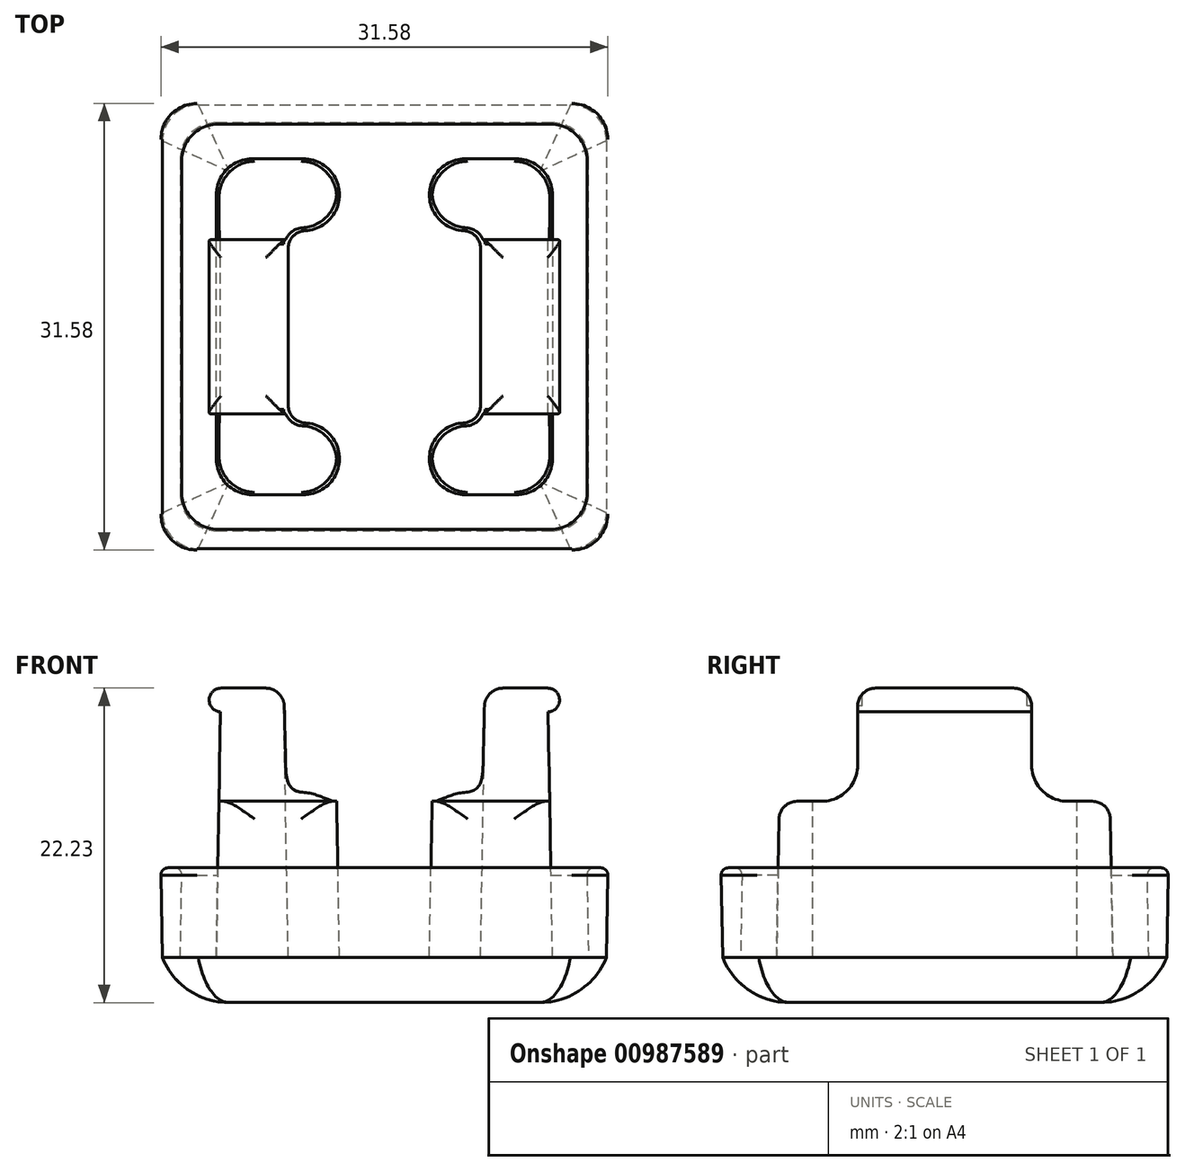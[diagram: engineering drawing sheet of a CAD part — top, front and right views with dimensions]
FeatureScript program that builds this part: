
annotation { "Feature Type Name" : "Feature", "Feature Type Description" : "" }
export const myFeature = defineFeature(function(context is Context, id is Id, definition is map)
    precondition{}
    {
        {
            var Q0;
            Q0=qCreatedBy(makeId("Top.planeOp"),FACE);
            var sketch = newSketch(context, id + "F0", { "sketchPlane" : qUnion([Q0])});
            skLineSegment(sketch, "E0.bottom", {"start": v(-15.68, 15.68) * mm, "end": v(15.68, 15.68) * mm});
            skLineSegment(sketch, "E0.top", {"start": v(-15.68, -15.68) * mm, "end": v(15.68, -15.68) * mm});
            skLineSegment(sketch, "E0.left", {"start": v(-15.68, 15.68) * mm, "end": v(-15.68, -15.68) * mm});
            skLineSegment(sketch, "E0.right", {"start": v(15.68, 15.68) * mm, "end": v(15.68, -15.68) * mm});
            skLineSegment(sketch, "E1.bottom", {"start": v(-14.41, 14.41) * mm, "end": v(14.41, 14.41) * mm});
            skLineSegment(sketch, "E1.top", {"start": v(-14.41, -14.41) * mm, "end": v(14.41, -14.41) * mm});
            skLineSegment(sketch, "E1.left", {"start": v(-14.41, 14.41) * mm, "end": v(-14.41, -14.41) * mm});
            skLineSegment(sketch, "E1.right", {"start": v(14.41, 14.41) * mm, "end": v(14.41, -14.41) * mm});
            skLineSegment(sketch, "E2.bottom", {"start": v(-11.87, 11.87) * mm, "end": v(-3.17, 11.87) * mm});
            skLineSegment(sketch, "E2.top", {"start": v(-11.87, -11.87) * mm, "end": v(-3.17, -11.87) * mm});
            skLineSegment(sketch, "E2.left", {"start": v(-11.87, 11.87) * mm, "end": v(-11.87, -11.87) * mm});
            skLineSegment(sketch, "E2.right", {"start": v(11.87, 11.87) * mm, "end": v(11.87, -11.87) * mm});
            skLineSegment(sketch, "E3.bottom", {"start": v(-6.8, 6.8) * mm, "end": v(-3.17, 6.8) * mm});
            skLineSegment(sketch, "E3.top", {"start": v(-6.8, -6.8) * mm, "end": v(-3.18, -6.8) * mm});
            skLineSegment(sketch, "E3.left", {"start": v(-6.8, 6.8) * mm, "end": v(-6.8, -6.8) * mm});
            skLineSegment(sketch, "E3.right", {"start": v(6.8, 6.8) * mm, "end": v(6.8, -6.8) * mm});
            skLineSegment(sketch, "E4", {"start": v(-3.17, 6.8) * mm, "end": v(-3.18, 11.87) * mm});
            skLineSegment(sketch, "E5", {"start": v(3.17, 11.87) * mm, "end": v(3.18, 6.8) * mm});
            skLineSegment(sketch, "E6", {"start": v(-3.18, -6.8) * mm, "end": v(-3.18, -11.87) * mm});
            skLineSegment(sketch, "E7", {"start": v(3.18, -6.8) * mm, "end": v(3.18, -11.87) * mm});
            skLineSegment(sketch, "E8.trimOffspring", {"start": v(3.18, 6.8) * mm, "end": v(6.8, 6.8) * mm});
            skLineSegment(sketch, "E9.trimOffspring", {"start": v(3.18, 11.87) * mm, "end": v(11.87, 11.87) * mm});
            skLineSegment(sketch, "E10.trimOffspring", {"start": v(3.18, -6.8) * mm, "end": v(6.8, -6.8) * mm});
            skLineSegment(sketch, "E11.trimOffspring", {"start": v(3.18, -11.87) * mm, "end": v(11.87, -11.87) * mm});
            skSolve(sketch);
        }
        {
            var Q0;
            Q0=makeQuery(id+"F0.imprint","IMPRINT",FACE,{"disambiguationData":[TD([[makeQuery(id+"F0.imprint","IMPRINT",EDGE,{"derivedFrom":sQuery(id+"F0.wireOp",EDGE,"E2.bottom")}),-1.0]])]});
            var Q1;
            Q1=makeQuery(id+"F0.imprint","IMPRINT",FACE,{"disambiguationData":[TD([[makeQuery(id+"F0.imprint","IMPRINT",EDGE,{"derivedFrom":sQuery(id+"F0.wireOp",EDGE,"E2.right")}),-1.0]])]});
            extrude(context, id + "F1", {"entities" : qUnion([Q0, Q1]), "depth" : 19.05 * mm, "offsetDistance" : 25.4 * mm, "hasDraft" : true, "draftAngle" : 1 * degree, "draftPullDirection" : true});
        }
        {
            var Q0;
            Q0 = qSketchRegion(id + "F0", true);
            extrude(context, id + "F2", {"entities" : qUnion([Q0]), "depth" : 6.35 * mm, "offsetDistance" : 25.4 * mm, "hasDraft" : true, "draftAngle" : 1 * degree});
        }
        {
            var Q0;
            Q0 = qSketchRegion(id + "F0", true);
            var Q1;
            Q1=makeQuery(id+"F0.imprint","IMPRINT",FACE,{"disambiguationData":[TD([[makeQuery(id+"F0.imprint","IMPRINT",EDGE,{"derivedFrom":sQuery(id+"F0.wireOp",EDGE,"E2.bottom")}),-1.0]])]});
            var Q2;
            Q2=makeQuery(id+"F0.imprint","IMPRINT",FACE,{"disambiguationData":[TD([[makeQuery(id+"F0.imprint","IMPRINT",EDGE,{"derivedFrom":sQuery(id+"F0.wireOp",EDGE,"E2.right")}),-1.0]])]});
            var Q3;
            Q3=makeQuery(id+"F0.imprint","IMPRINT",FACE,{"disambiguationData":[TD([[makeQuery(id+"F0.imprint","IMPRINT",EDGE,{"derivedFrom":sQuery(id+"F0.wireOp",EDGE,"E1.bottom")}),-1.0]])]});
            extrude(context, id + "F3", {"entities" : qUnion([Q0, Q1, Q2, Q3]), "oppositeDirection" : true, "depth" : 3.17 * mm, "offsetDistance" : 25.4 * mm});
        }
        {
            var Q0;
            Q0=makeQuery(id+"F1.opExtrude","SWEPT_EDGE",EDGE,{"disambiguationData":[OSD([sQuery(id+"F0.wireOp",EDGE,"E2.bottom"),sQuery(id+"F0.wireOp",EDGE,"E2.left")])]});
            var Q1;
            Q1=makeQuery(id+"F1.opExtrude","SWEPT_EDGE",EDGE,{"disambiguationData":[OSD([sQuery(id+"F0.wireOp",EDGE,"E2.right"),sQuery(id+"F0.wireOp",EDGE,"E9.trimOffspring")])]});
            var Q2;
            Q2=makeQuery(id+"F1.opExtrude","SWEPT_EDGE",EDGE,{"disambiguationData":[OSD([sQuery(id+"F0.wireOp",EDGE,"E2.top"),sQuery(id+"F0.wireOp",EDGE,"E2.left")])]});
            var Q3;
            Q3=makeQuery(id+"F1.opExtrude","SWEPT_EDGE",EDGE,{"disambiguationData":[OSD([sQuery(id+"F0.wireOp",EDGE,"E2.right"),sQuery(id+"F0.wireOp",EDGE,"E11.trimOffspring")])]});
            var Q4;
            Q4=makeQuery(id+"F1.opExtrude","SWEPT_EDGE",EDGE,{"disambiguationData":[OSD([sQuery(id+"F0.wireOp",EDGE,"E7"),sQuery(id+"F0.wireOp",EDGE,"E11.trimOffspring")])]});
            var Q5;
            Q5=makeQuery(id+"F1.opExtrude","SWEPT_EDGE",EDGE,{"disambiguationData":[OSD([sQuery(id+"F0.wireOp",EDGE,"E2.top"),sQuery(id+"F0.wireOp",EDGE,"E6")])]});
            var Q6;
            Q6=makeQuery(id+"F1.opExtrude","SWEPT_EDGE",EDGE,{"disambiguationData":[OSD([sQuery(id+"F0.wireOp",EDGE,"E7"),sQuery(id+"F0.wireOp",EDGE,"E10.trimOffspring")])]});
            var Q7;
            Q7=makeQuery(id+"F1.opExtrude","SWEPT_EDGE",EDGE,{"disambiguationData":[OSD([sQuery(id+"F0.wireOp",EDGE,"E5"),sQuery(id+"F0.wireOp",EDGE,"E8.trimOffspring")])]});
            var Q8;
            Q8=makeQuery(id+"F1.opExtrude","SWEPT_EDGE",EDGE,{"disambiguationData":[OSD([sQuery(id+"F0.wireOp",EDGE,"E5"),sQuery(id+"F0.wireOp",EDGE,"E9.trimOffspring")])]});
            var Q9;
            Q9=makeQuery(id+"F1.opExtrude","SWEPT_EDGE",EDGE,{"disambiguationData":[OSD([sQuery(id+"F0.wireOp",EDGE,"E3.top"),sQuery(id+"F0.wireOp",EDGE,"E6")])]});
            var Q10;
            Q10=makeQuery(id+"F1.opExtrude","SWEPT_EDGE",EDGE,{"disambiguationData":[OSD([sQuery(id+"F0.wireOp",EDGE,"E3.bottom"),sQuery(id+"F0.wireOp",EDGE,"E4")])]});
            var Q11;
            Q11=makeQuery(id+"F1.opExtrude","SWEPT_EDGE",EDGE,{"disambiguationData":[OSD([sQuery(id+"F0.wireOp",EDGE,"E2.bottom"),sQuery(id+"F0.wireOp",EDGE,"E4")])]});
            var Q12;
            Q12=makeQuery(id+"F2.opExtrude","SWEPT_EDGE",EDGE,{"disambiguationData":[OSD([sQuery(id+"F0.wireOp",EDGE,"E0.bottom"),sQuery(id+"F0.wireOp",EDGE,"E0.left")])]});
            var Q13;
            Q13=makeQuery(id+"F2.opExtrude","SWEPT_EDGE",EDGE,{"disambiguationData":[OSD([sQuery(id+"F0.wireOp",EDGE,"E0.top"),sQuery(id+"F0.wireOp",EDGE,"E0.left")])]});
            var Q14;
            Q14=makeQuery(id+"F3.opExtrude","SWEPT_EDGE",EDGE,{"disambiguationData":[OSD([sQuery(id+"F0.wireOp",EDGE,"E0.bottom"),sQuery(id+"F0.wireOp",EDGE,"E0.left")])]});
            var Q15;
            Q15=makeQuery(id+"F3.opExtrude","SWEPT_EDGE",EDGE,{"disambiguationData":[OSD([sQuery(id+"F0.wireOp",EDGE,"E0.top"),sQuery(id+"F0.wireOp",EDGE,"E0.left")])]});
            var Q16;
            Q16=makeQuery(id+"F3.opExtrude","SWEPT_EDGE",EDGE,{"disambiguationData":[OSD([sQuery(id+"F0.wireOp",EDGE,"E0.top"),sQuery(id+"F0.wireOp",EDGE,"E0.right")])]});
            var Q17;
            Q17=makeQuery(id+"F2.opExtrude","SWEPT_EDGE",EDGE,{"disambiguationData":[OSD([sQuery(id+"F0.wireOp",EDGE,"E0.top"),sQuery(id+"F0.wireOp",EDGE,"E0.right")])]});
            var Q18;
            Q18=makeQuery(id+"F3.opExtrude","SWEPT_EDGE",EDGE,{"disambiguationData":[OSD([sQuery(id+"F0.wireOp",EDGE,"E0.bottom"),sQuery(id+"F0.wireOp",EDGE,"E0.right")])]});
            var Q19;
            Q19=makeQuery(id+"F2.opExtrude","SWEPT_EDGE",EDGE,{"disambiguationData":[OSD([sQuery(id+"F0.wireOp",EDGE,"E0.bottom"),sQuery(id+"F0.wireOp",EDGE,"E0.right")])]});
            var Q20;
            Q20=makeQuery(id+"F2.opExtrude","SWEPT_EDGE",EDGE,{"disambiguationData":[OSD([sQuery(id+"F0.wireOp",EDGE,"E1.top"),sQuery(id+"F0.wireOp",EDGE,"E1.left")])]});
            var Q21;
            Q21=makeQuery(id+"F2.opExtrude","SWEPT_EDGE",EDGE,{"disambiguationData":[OSD([sQuery(id+"F0.wireOp",EDGE,"E1.top"),sQuery(id+"F0.wireOp",EDGE,"E1.right")])]});
            var Q22;
            Q22=makeQuery(id+"F2.opExtrude","SWEPT_EDGE",EDGE,{"disambiguationData":[OSD([sQuery(id+"F0.wireOp",EDGE,"E1.bottom"),sQuery(id+"F0.wireOp",EDGE,"E1.right")])]});
            var Q23;
            Q23=makeQuery(id+"F2.opExtrude","SWEPT_EDGE",EDGE,{"disambiguationData":[OSD([sQuery(id+"F0.wireOp",EDGE,"E1.bottom"),sQuery(id+"F0.wireOp",EDGE,"E1.left")])]});
            fillet(context, id + "F4", {"entities" : qUnion([Q0, Q1, Q2, Q3, Q4, Q5, Q6, Q7, Q8, Q9, Q10, Q11, Q12, Q13, Q14, Q15, Q16, Q17, Q18, Q19, Q20, Q21, Q22, Q23]), "radius" : 2.54 * mm, "tangentPropagation" : true, "allowEdgeOverflow" : false});
        }
        {
            var Q0;
            Q0=makeQuery(id+"F1.opExtrude","SWEPT_EDGE",EDGE,{"disambiguationData":[OSD([sQuery(id+"F0.wireOp",EDGE,"E3.bottom"),sQuery(id+"F0.wireOp",EDGE,"E3.left")])]});
            var Q1;
            Q1=makeQuery(id+"F1.opExtrude","SWEPT_EDGE",EDGE,{"disambiguationData":[OSD([sQuery(id+"F0.wireOp",EDGE,"E3.top"),sQuery(id+"F0.wireOp",EDGE,"E3.left")])]});
            var Q2;
            Q2=makeQuery(id+"F1.opExtrude","SWEPT_EDGE",EDGE,{"disambiguationData":[OSD([sQuery(id+"F0.wireOp",EDGE,"E3.right"),sQuery(id+"F0.wireOp",EDGE,"E8.trimOffspring")])]});
            var Q3;
            Q3=makeQuery(id+"F1.opExtrude","SWEPT_EDGE",EDGE,{"disambiguationData":[OSD([sQuery(id+"F0.wireOp",EDGE,"E3.right"),sQuery(id+"F0.wireOp",EDGE,"E10.trimOffspring")])]});
            fillet(context, id + "F5", {"entities" : qUnion([Q0, Q1, Q2, Q3]), "radius" : 1.27 * mm, "tangentPropagation" : true, "allowEdgeOverflow" : false});
        }
        {
            var Q0;
            Q0=qCreatedBy(makeId("Right.planeOp"),FACE);
            var sketch = newSketch(context, id + "F6", { "sketchPlane" : qUnion([Q0])});
            skLineSegment(sketch, "E12.bottom", {"start": v(-15.85, 21.25) * mm, "end": v(-6.15, 21.25) * mm});
            skLineSegment(sketch, "E12.top", {"start": v(-15.85, 11.05) * mm, "end": v(-8.69, 11.05) * mm});
            skLineSegment(sketch, "E12.left", {"start": v(-15.85, 21.25) * mm, "end": v(-15.85, 11.05) * mm});
            skLineSegment(sketch, "E12.right", {"start": v(-6.15, 21.25) * mm, "end": v(-6.15, 13.59) * mm});
            skLineSegment(sketch, "E13.bottom", {"start": v(15.85, 21.25) * mm, "end": v(6.15, 21.25) * mm});
            skLineSegment(sketch, "E13.top", {"start": v(15.85, 11.05) * mm, "end": v(8.69, 11.05) * mm});
            skLineSegment(sketch, "E13.left", {"start": v(15.85, 21.25) * mm, "end": v(15.85, 11.05) * mm});
            skLineSegment(sketch, "E13.right", {"start": v(6.15, 21.25) * mm, "end": v(6.15, 13.59) * mm});
            skPoint(sketch, "E14.visualSharp", {"position": v(-6.15, 11.05) * mm});
            skArc(sketch, "E14.filletArc", {"start": v(-8.69, 11.05) * mm, "mid": v(-6.9, 11.8) * mm, "end": v(-6.15, 13.59) * mm});
            skPoint(sketch, "E15.visualSharp", {"position": v(6.15, 11.05) * mm});
            skArc(sketch, "E15.filletArc", {"start": v(6.15, 13.59) * mm, "mid": v(6.9, 11.8) * mm, "end": v(8.69, 11.05) * mm});
            skSolve(sketch);
        }
        {
            var Q0;
            Q0=makeQuery(id+"F6.imprint","IMPRINT",FACE,{"disambiguationData":[TD([[makeQuery(id+"F6.imprint","IMPRINT",EDGE,{"derivedFrom":sQuery(id+"F6.wireOp",EDGE,"E12.bottom")}),-1.0]])]});
            var Q1;
            Q1=makeQuery(id+"F6.imprint","IMPRINT",FACE,{"disambiguationData":[TD([[makeQuery(id+"F6.imprint","IMPRINT",EDGE,{"derivedFrom":sQuery(id+"F6.wireOp",EDGE,"E13.bottom")}),1.0]])]});
            extrude(context, id + "F7", {"entities" : qUnion([Q0, Q1]), "depth" : 25.4 * mm, "offsetDistance" : 25.4 * mm, "hasSecondDirection" : true, "secondDirectionOppositeDirection" : true, "secondDirectionDepth" : 25.4 * mm});
        }
        {
            var Q0;
            Q0=makeQuery(id+"F7.opExtrude","SWEPT_BODY",BODY,{"disambiguationData":[OSD([sQuery(id+"F6.wireOp",EDGE,"E12.bottom"),sQuery(id+"F6.wireOp",EDGE,"E12.top"),sQuery(id+"F6.wireOp",EDGE,"E12.left"),sQuery(id+"F6.wireOp",EDGE,"E12.right"),sQuery(id+"F6.wireOp",EDGE,"E14.filletArc")])]});
            var Q1;
            Q1=makeQuery(id+"F7.opExtrude","SWEPT_BODY",BODY,{"disambiguationData":[OSD([sQuery(id+"F6.wireOp",EDGE,"E13.bottom"),sQuery(id+"F6.wireOp",EDGE,"E13.top"),sQuery(id+"F6.wireOp",EDGE,"E13.left"),sQuery(id+"F6.wireOp",EDGE,"E13.right"),sQuery(id+"F6.wireOp",EDGE,"E15.filletArc")])]});
            var Q2;
            Q2=makeQuery(id+"F1.opExtrude","SWEPT_BODY",BODY,{"disambiguationData":[OSD([sQuery(id+"F0.wireOp",EDGE,"E2.right"),sQuery(id+"F0.wireOp",EDGE,"E3.right"),sQuery(id+"F0.wireOp",EDGE,"E5"),sQuery(id+"F0.wireOp",EDGE,"E7"),sQuery(id+"F0.wireOp",EDGE,"E8.trimOffspring"),sQuery(id+"F0.wireOp",EDGE,"E9.trimOffspring"),sQuery(id+"F0.wireOp",EDGE,"E10.trimOffspring"),sQuery(id+"F0.wireOp",EDGE,"E11.trimOffspring")])]});
            var Q3;
            Q3=makeQuery(id+"F1.opExtrude","SWEPT_BODY",BODY,{"disambiguationData":[OSD([sQuery(id+"F0.wireOp",EDGE,"E2.bottom"),sQuery(id+"F0.wireOp",EDGE,"E2.top"),sQuery(id+"F0.wireOp",EDGE,"E2.left"),sQuery(id+"F0.wireOp",EDGE,"E3.bottom"),sQuery(id+"F0.wireOp",EDGE,"E3.top"),sQuery(id+"F0.wireOp",EDGE,"E3.left"),sQuery(id+"F0.wireOp",EDGE,"E4"),sQuery(id+"F0.wireOp",EDGE,"E6")])]});
            booleanBodies(context, id + "F8", {"operationType" : BooleanOperationType.SUBTRACTION, "tools" : qUnion([Q0, Q1]), "targets" : qUnion([Q2, Q3])});
        }
        {
            var Q0;
            Q0=qCreatedBy(makeId("Front.planeOp"),FACE);
            var sketch = newSketch(context, id + "F9", { "sketchPlane" : qUnion([Q0])});
            skArc(sketch, "E16", {"start": v(11.57, 17.37) * mm, "mid": v(12.38, 18.22) * mm, "end": v(11.54, 19.05) * mm});
            skLineSegment(sketch, "E17", {"start": v(11.57, 17.37) * mm, "end": v(11.54, 19.05) * mm});
            skSolve(sketch);
        }
        {
            var Q0;
            Q0=makeQuery(id+"F9.imprint","IMPRINT",FACE,{"disambiguationData":[TD([[makeQuery(id+"F9.imprint","IMPRINT",EDGE,{"derivedFrom":sQuery(id+"F9.wireOp",EDGE,"E16")}),1.0]])]});
            extrude(context, id + "F10", {"entities" : qUnion([Q0]), "depth" : 6.15 * mm, "offsetDistance" : 25.4 * mm, "hasSecondDirection" : true, "secondDirectionOppositeDirection" : true, "secondDirectionDepth" : 6.15 * mm});
        }
        {
            var Q0;
            Q0=makeQuery(id+"F10.opExtrude","SWEPT_BODY",BODY,{"disambiguationData":[OSD([sQuery(id+"F9.wireOp",EDGE,"E16"),sQuery(id+"F9.wireOp",EDGE,"E17")])]});
            var Q1;
            Q1=qCreatedBy(makeId("Right.planeOp"),FACE);
            mirror(context, id + "F11", {"operationType" : NewBodyOperationType.ADD, "entities" : qUnion([Q0]), "mirrorPlane" : qUnion([Q1])});
        }
        {
            var Q0;
            Q0=makeQuery(id+"F8.opBoolean","INTERSECT",EDGE,{"derivedFrom":[makeQuery(id+"F1.opExtrude","CAP_FACE",FACE,{"disambiguationData":[OSD([sQuery(id+"F0.wireOp",EDGE,"E2.bottom"),sQuery(id+"F0.wireOp",EDGE,"E2.top"),sQuery(id+"F0.wireOp",EDGE,"E2.left"),sQuery(id+"F0.wireOp",EDGE,"E3.bottom"),sQuery(id+"F0.wireOp",EDGE,"E3.top"),sQuery(id+"F0.wireOp",EDGE,"E3.left"),sQuery(id+"F0.wireOp",EDGE,"E4"),sQuery(id+"F0.wireOp",EDGE,"E6")])],"isStart":false}),makeQuery(id+"F7.opExtrude","SWEPT_FACE",FACE,{"disambiguationData":[OSD([sQuery(id+"F6.wireOp",EDGE,"E12.right")])]})]});
            var Q1;
            Q1=makeQuery(id+"F1.opExtrude","CAP_EDGE",EDGE,{"disambiguationData":[OSD([sQuery(id+"F0.wireOp",EDGE,"E3.left")])],"isStart":false});
            var Q2;
            Q2=makeQuery(id+"F8.opBoolean","INTERSECT",EDGE,{"derivedFrom":[makeQuery(id+"F1.opExtrude","CAP_FACE",FACE,{"disambiguationData":[OSD([sQuery(id+"F0.wireOp",EDGE,"E2.bottom"),sQuery(id+"F0.wireOp",EDGE,"E2.top"),sQuery(id+"F0.wireOp",EDGE,"E2.left"),sQuery(id+"F0.wireOp",EDGE,"E3.bottom"),sQuery(id+"F0.wireOp",EDGE,"E3.top"),sQuery(id+"F0.wireOp",EDGE,"E3.left"),sQuery(id+"F0.wireOp",EDGE,"E4"),sQuery(id+"F0.wireOp",EDGE,"E6")])],"isStart":false}),makeQuery(id+"F7.opExtrude","SWEPT_FACE",FACE,{"disambiguationData":[OSD([sQuery(id+"F6.wireOp",EDGE,"E13.right")])]})]});
            var Q3;
            Q3=makeQuery(id+"F8.opBoolean","INTERSECT",EDGE,{"derivedFrom":[makeQuery(id+"F1.opExtrude","CAP_FACE",FACE,{"disambiguationData":[OSD([sQuery(id+"F0.wireOp",EDGE,"E2.right"),sQuery(id+"F0.wireOp",EDGE,"E3.right"),sQuery(id+"F0.wireOp",EDGE,"E5"),sQuery(id+"F0.wireOp",EDGE,"E7"),sQuery(id+"F0.wireOp",EDGE,"E8.trimOffspring"),sQuery(id+"F0.wireOp",EDGE,"E9.trimOffspring"),sQuery(id+"F0.wireOp",EDGE,"E10.trimOffspring"),sQuery(id+"F0.wireOp",EDGE,"E11.trimOffspring")])],"isStart":false}),makeQuery(id+"F7.opExtrude","SWEPT_FACE",FACE,{"disambiguationData":[OSD([sQuery(id+"F6.wireOp",EDGE,"E12.right")])]})]});
            var Q4;
            Q4=makeQuery(id+"F1.opExtrude","CAP_EDGE",EDGE,{"disambiguationData":[OSD([sQuery(id+"F0.wireOp",EDGE,"E3.right")])],"isStart":false});
            var Q5;
            Q5=makeQuery(id+"F8.opBoolean","INTERSECT",EDGE,{"derivedFrom":[makeQuery(id+"F1.opExtrude","CAP_FACE",FACE,{"disambiguationData":[OSD([sQuery(id+"F0.wireOp",EDGE,"E2.right"),sQuery(id+"F0.wireOp",EDGE,"E3.right"),sQuery(id+"F0.wireOp",EDGE,"E5"),sQuery(id+"F0.wireOp",EDGE,"E7"),sQuery(id+"F0.wireOp",EDGE,"E8.trimOffspring"),sQuery(id+"F0.wireOp",EDGE,"E9.trimOffspring"),sQuery(id+"F0.wireOp",EDGE,"E10.trimOffspring"),sQuery(id+"F0.wireOp",EDGE,"E11.trimOffspring")])],"isStart":false}),makeQuery(id+"F7.opExtrude","SWEPT_FACE",FACE,{"disambiguationData":[OSD([sQuery(id+"F6.wireOp",EDGE,"E13.right")])]})]});
            fillet(context, id + "F12", {"entities" : qUnion([Q0, Q1, Q2, Q3, Q4, Q5]), "radius" : 1.27 * mm, "tangentPropagation" : true, "allowEdgeOverflow" : false});
        }
        {
            var Q0;
            Q0=makeQuery(id+"F8.opBoolean","INTERSECT",EDGE,{"derivedFrom":[makeQuery(id+"F1.opExtrude","SWEPT_FACE",FACE,{"disambiguationData":[OSD([sQuery(id+"F0.wireOp",EDGE,"E2.top")])]}),makeQuery(id+"F7.opExtrude","SWEPT_FACE",FACE,{"disambiguationData":[OSD([sQuery(id+"F6.wireOp",EDGE,"E12.top")])]})]});
            var Q1;
            Q1=makeQuery(id+"F8.opBoolean","INTERSECT",EDGE,{"derivedFrom":[makeQuery(id+"F1.opExtrude","SWEPT_FACE",FACE,{"disambiguationData":[OSD([sQuery(id+"F0.wireOp",EDGE,"E11.trimOffspring")])]}),makeQuery(id+"F7.opExtrude","SWEPT_FACE",FACE,{"disambiguationData":[OSD([sQuery(id+"F6.wireOp",EDGE,"E12.top")])]})]});
            var Q2;
            Q2=makeQuery(id+"F8.opBoolean","INTERSECT",EDGE,{"derivedFrom":[makeQuery(id+"F1.opExtrude","SWEPT_FACE",FACE,{"disambiguationData":[OSD([sQuery(id+"F0.wireOp",EDGE,"E9.trimOffspring")])]}),makeQuery(id+"F7.opExtrude","SWEPT_FACE",FACE,{"disambiguationData":[OSD([sQuery(id+"F6.wireOp",EDGE,"E13.top")])]})]});
            var Q3;
            Q3=makeQuery(id+"F8.opBoolean","INTERSECT",EDGE,{"derivedFrom":[makeQuery(id+"F1.opExtrude","SWEPT_FACE",FACE,{"disambiguationData":[OSD([sQuery(id+"F0.wireOp",EDGE,"E2.bottom")])]}),makeQuery(id+"F7.opExtrude","SWEPT_FACE",FACE,{"disambiguationData":[OSD([sQuery(id+"F6.wireOp",EDGE,"E13.top")])]})]});
            fillet(context, id + "F13", {"entities" : qUnion([Q0, Q1, Q2, Q3]), "radius" : 1.27 * mm, "allowEdgeOverflow" : false});
        }
        {
            var Q0;
            Q0=makeQuery(id+"F3.opExtrude","CAP_EDGE",EDGE,{"disambiguationData":[OSD([sQuery(id+"F0.wireOp",EDGE,"E0.top")])],"isStart":false});
            var Q1;
            Q1=makeQuery(id+"F3.opExtrude","CAP_EDGE",EDGE,{"disambiguationData":[OSD([sQuery(id+"F0.wireOp",EDGE,"E0.left")])],"isStart":false});
            fillet(context, id + "F14", {"entities" : qUnion([Q0, Q1]), "radius" : 5.08 * mm, "tangentPropagation" : true, "allowEdgeOverflow" : false});
        }
        {
            var Q0;
            Q0=makeQuery(id+"F2.opExtrude","CAP_EDGE",EDGE,{"disambiguationData":[OSD([sQuery(id+"F0.wireOp",EDGE,"E0.left")])],"isStart":false});
            var Q1;
            Q1=makeQuery(id+"F2.opExtrude","CAP_EDGE",EDGE,{"disambiguationData":[OSD([sQuery(id+"F0.wireOp",EDGE,"E1.left")])],"isStart":false});
            fillet(context, id + "F15", {"entities" : qUnion([Q0, Q1]), "radius" : 0.5 * mm, "tangentPropagation" : true, "allowEdgeOverflow" : false});
        }
    });
